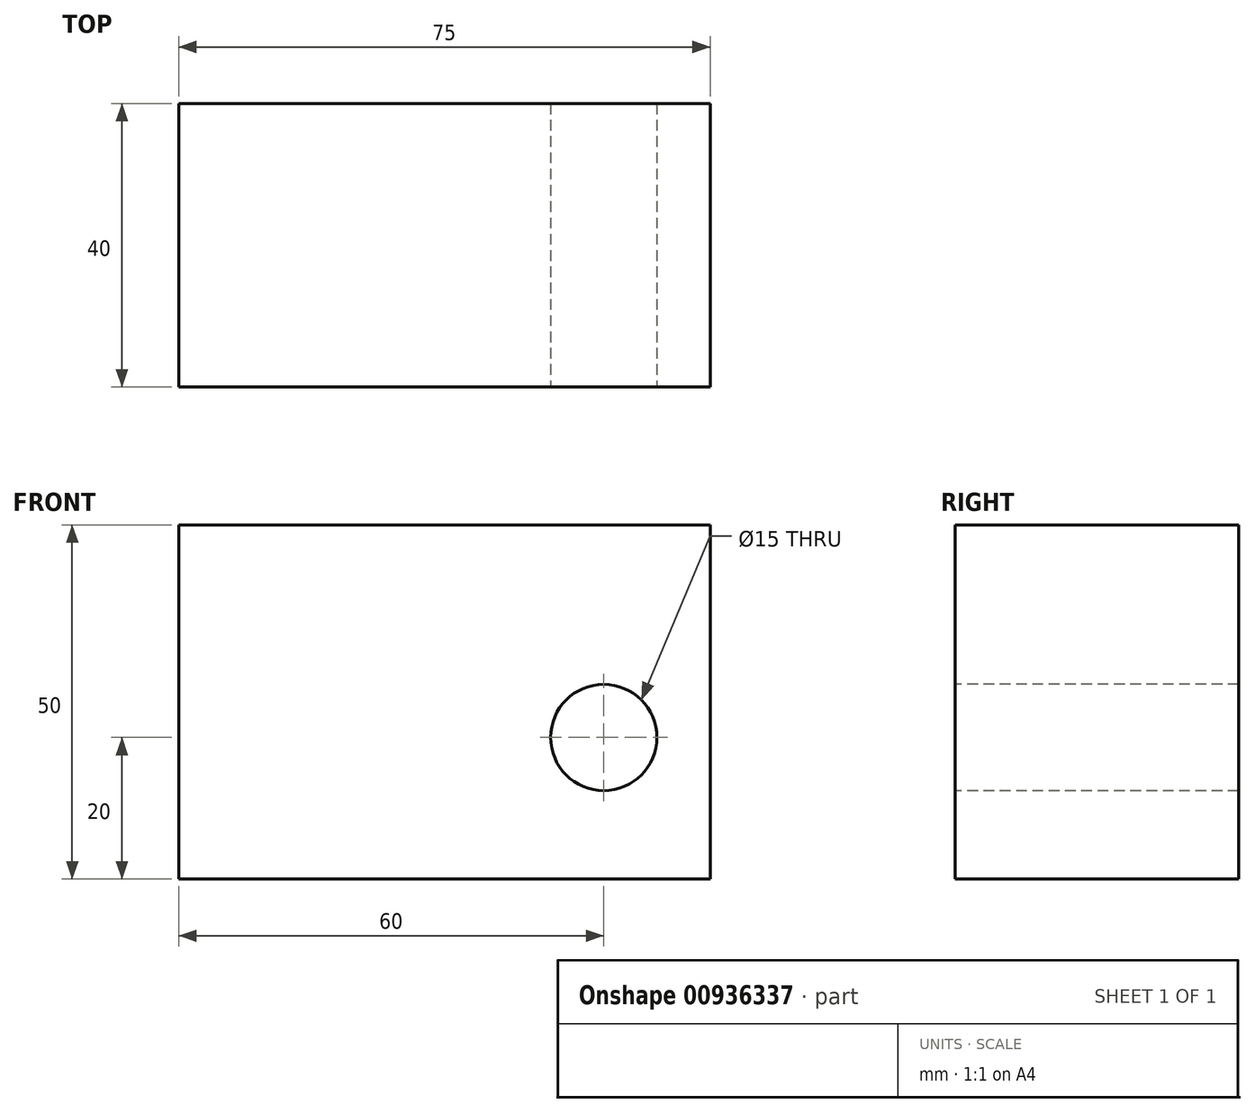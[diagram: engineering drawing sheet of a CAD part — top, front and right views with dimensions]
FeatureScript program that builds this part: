
annotation { "Feature Type Name" : "Feature", "Feature Type Description" : "" }
export const myFeature = defineFeature(function(context is Context, id is Id, definition is map)
    precondition{}
    {
        {
            var Q0;
            Q0=qCreatedBy(makeId("Front.planeOp"),FACE);
            var sketch = newSketch(context, id + "F0", { "sketchPlane" : qUnion([Q0])});
            skLineSegment(sketch, "E0", {"start": v(0, -20) * mm, "end": v(15, -20) * mm});
            skLineSegment(sketch, "E1", {"start": v(15, -20) * mm, "end": v(15, 0) * mm});
            skLineSegment(sketch, "E2", {"start": v(15, 0) * mm, "end": v(15, 30) * mm});
            skLineSegment(sketch, "E3", {"start": v(15, 30) * mm, "end": v(-60, 30) * mm});
            skLineSegment(sketch, "E4", {"start": v(-60, 30) * mm, "end": v(-60, -20) * mm});
            skLineSegment(sketch, "E5", {"start": v(-60, -20) * mm, "end": v(0, -20) * mm});
            skSolve(sketch);
        }
        {
            var Q0;
            Q0=makeQuery(id+"F0.imprint","IMPRINT",FACE,{"disambiguationData":[TD([[makeQuery(id+"F0.imprint","IMPRINT",EDGE,{"derivedFrom":sQuery(id+"F0.wireOp",EDGE,"E0")}),1.0]])]});
            extrude(context, id + "F1", {"entities" : qUnion([Q0]), "depth" : 40 * mm, "offsetDistance" : 25 * mm, "symmetric" : true});
        }
        {
            var Q0;
            Q0=makeQuery(id+"F1.opExtrude","CAP_FACE",FACE,{"disambiguationData":[OSD([sQuery(id+"F0.wireOp",EDGE,"E0"),sQuery(id+"F0.wireOp",EDGE,"E1"),sQuery(id+"F0.wireOp",EDGE,"E2"),sQuery(id+"F0.wireOp",EDGE,"E3"),sQuery(id+"F0.wireOp",EDGE,"E4"),sQuery(id+"F0.wireOp",EDGE,"E5")])],"isStart":false});
            var sketch = newSketch(context, id + "F2", { "sketchPlane" : qUnion([Q0])});
            skCircle(sketch, "E6", {"center": v(0, 0) * mm, "radius": 7.5 * mm});
            skSolve(sketch);
        }
        {
            var Q0;
            Q0=makeQuery(id+"F2.imprint","IMPRINT",FACE,{"disambiguationData":[TD([[makeQuery(id+"F2.imprint","IMPRINT",EDGE,{"derivedFrom":sQuery(id+"F2.wireOp",EDGE,"E6")}),1.0]])]});
            var Q1;
            Q1=makeQuery(id+"F1.opExtrude","CAP_FACE",FACE,{"disambiguationData":[OSD([sQuery(id+"F0.wireOp",EDGE,"E0"),sQuery(id+"F0.wireOp",EDGE,"E1"),sQuery(id+"F0.wireOp",EDGE,"E2"),sQuery(id+"F0.wireOp",EDGE,"E3"),sQuery(id+"F0.wireOp",EDGE,"E4"),sQuery(id+"F0.wireOp",EDGE,"E5")])],"isStart":true});
            extrude(context, id + "F3", {"entities" : qUnion([Q0]), "operationType" : NewBodyOperationType.REMOVE, "endBound" : BoundingType.UP_TO_SURFACE, "oppositeDirection" : true, "depth" : 25 * mm, "endBoundEntityFace" : qUnion([Q1]), "offsetDistance" : 25 * mm});
        }
    });
